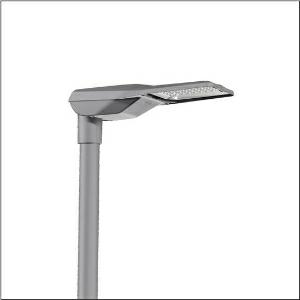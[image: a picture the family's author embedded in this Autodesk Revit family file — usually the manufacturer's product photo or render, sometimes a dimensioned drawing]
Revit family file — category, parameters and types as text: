
# Revit family: streetlight_sl_21_iq_mini___st0_5a_5xe2b31d08gb_9f53
name_source: partatom
category: Lighting Fixtures
units: mm (PartAtom-declared; Revit-internal decimal feet)

## family parameters
Cut with Voids When Loaded = No
Host = Face
Light Source = No
Part Type = Normal
Room Calculation Point = No
Round Connector Dimension = Use Diameter
Shared = No

## types (1)
- --- (1 x LED, 5680 lm, 37.1 W, 3000K)
    Apparent Load = 37 VA
    CIE Flux Codes = 41 75 97 100 100
    Color Rendering = 70
    Color Temperature = 3000K
    Default Elevation = 1800 mm
    Description = Streetlight SL 21 iQ mini, mast luminaire, primary light control with lens, of PMMA, primary optical cover: cover, of toughened safety glass, transparent, light distribution: ST0.5a, light emission: direct distribution, primary light characteristic: asymmetric, installation type: post-top, side-entry, LED, High Power LED, rated luminous flux: 5.680lm, luminous efficacy: 153lm/W, light colour: 730, colour temperature: 3000K, control gear: iQ-Comfort, control: Auto-Match, Temp-Guard, Lumen-Switch, Night-Set, Smart-Wire, Light-Fading, Desk-Remote (wireless, voltage-free reading and setting of iQ features in the workshop via application-optimized NFC function/RFID function), optimised constant luminous flux control (CLO 2.0), pre-setting: linear dimming characteristic, mains connection: 220..240V, AC, 50/60Hz, start of lifetime: 37W, end of service life: 39W, reduction: 18W, luminaire housing, of diecast aluminium, powder-coated, Siteco® metallic grey (DB 702S), corrosivity category C5 mid according to DIN EN ISO 12944, please order mast flange separately, inclination adjustable: 0°, 5°, 10°, 15°, sealing non-destructively replaceable, multi-level sealing system, length: 628mm, width: 235mm, height: 110mm, mast flange for spigot size: 42mm (side-entry): 5XC10008XM4, 60/48mm (side-entry/post-top): 5XC10108XM2, 76/60mm (side-entry/post-top): 5XC10108XM1, mounting height: 4..8m, protection rating (complete): IP66, insulation class (complete): insulation class II (safety insulation), certification: CE, ENEC, ENEC+, VDE, impact resistance: IK10, permissible operating ambient temperature for outdoor applications: -40..+50°C, standard-compliant lighting for roads and squares, packaging unit: 1 piece

Light Distribution: ST0.5a
    Height = 110 mm
    Lamp = 1 x LED
    Lamp Light Flux = 5680 lm
    Lamp Power = 37.1 W
    Lamp count = 1
    Length = 625 mm
    Luminous efficacy = 153 lm/W
    Manufacturer = Siteco
    ModVariant = No
    Model = 5XE2B31D08GB
    Number of Poles = 1
    OnlyDefault = Yes
    Power Factor = 1
    Product Name = Streetlight SL 21 iQ mini | ST0.5a
    Product group = mast luminaire | pylon top
    ProductGroupID = 6100
    Protection Class = Protection class II
    Protection Degree = IP 66
    RLX_Detail_Level = 1
    RLX_Emergency_Light_Flux = 0 lm
    RLX_Emergency_Type = 0
    RLX_Emergency_Type_DB = No
    RlxData = <blob elided: 37377 chars, md5=d7af7ee6>
    Socket = socket
    Standby Power = 0 W
    System Light Flux = 5680 lm
    System Power = 37 W
    Type Comments = factory setting: luminous flux: 100 % | dim-lin: 254 | 385 mA
    Type Image = l_1003519.jpg
    URL = http://relux.com
    VarID = @adj_212713
    Voltage = 0 V
    Weight = 0.00 kg
    Width = 234 mm

## geometry (parser evidence)
native form markers: Blend x4, Sweep x12
no freeform markers — native parametric forms only
